# Revit family: Shower-Digital_Valve-KOHLER-DTV-K-528_1
name_source: partatom
category: Plumbing Fixtures
revit_build: Autodesk Revit 2017 (Build: 20160225_1515(x64)
units: mm (PartAtom-declared; Revit-internal decimal feet)

## family parameters
Cut with Voids When Loaded = No
Host = Face
OmniClass Number = 23.31.25.00
Part Type = Normal
Room Calculation Point = No
Round Connector Dimension = Use Diameter
Shared = No

## types (2) — shared parameters
ADA Compliant = No
Apparent Load = 1800 VA
Assembly Code = C1030200
CW Connection = Yes
Cold Water Inlet = Cold Water Inlet
Date Modified = 02/13/2020
Default Elevation = 42"
Drain Included = No
Electrical Connector = Yes
Electrical Note = One circuit required, protected with Class A Ground-Fault Circuit-Interrupter (GFCI). Outside North America, this device may be known as a Residual Current Device (RCD)
Finish = Kohler-Plastic-7-Black_Black
Flow Rate = 13 GPM
HW Connection = Yes
Height = 2 11/16"
Hot Water Inlet = Hot Water Inlet
Length = 13 3/8"
Manufacturer = KOHLER Co.
MasterFormat 1995 = 10820
MasterFormat 2004 = 10.28.13
Material = Thermoplastic
Pressure = 45.00 psi
Product Documentation Link = https://www.us.kohler.com
Product Page URL = http://www.us.kohler.com
Tempered Water Outlet 1 = Tempered Water Outlet 1
Tempered Water Outlet 2 = Tempered Water Outlet 2
URL = https://www.us.kohler.com
Voltage = 120 V
Waste Water Outlet = Waste Water Outlet
WaterSense Certified = No
Width = 12 1/2"

## per-type parameters (varying)
| type | Description | Model | Product Name | Type |
| K1, DTV+ | Digital two-port thermostatic valve | K-528-K1-NA | DTV+ | 1 |
| PM, DTV | Two-port digital thermostatic valve | K-528-PM-NA | DTV | 2 |

## geometry (parser evidence)
native form markers: Sweep x5
no freeform markers — native parametric forms only
